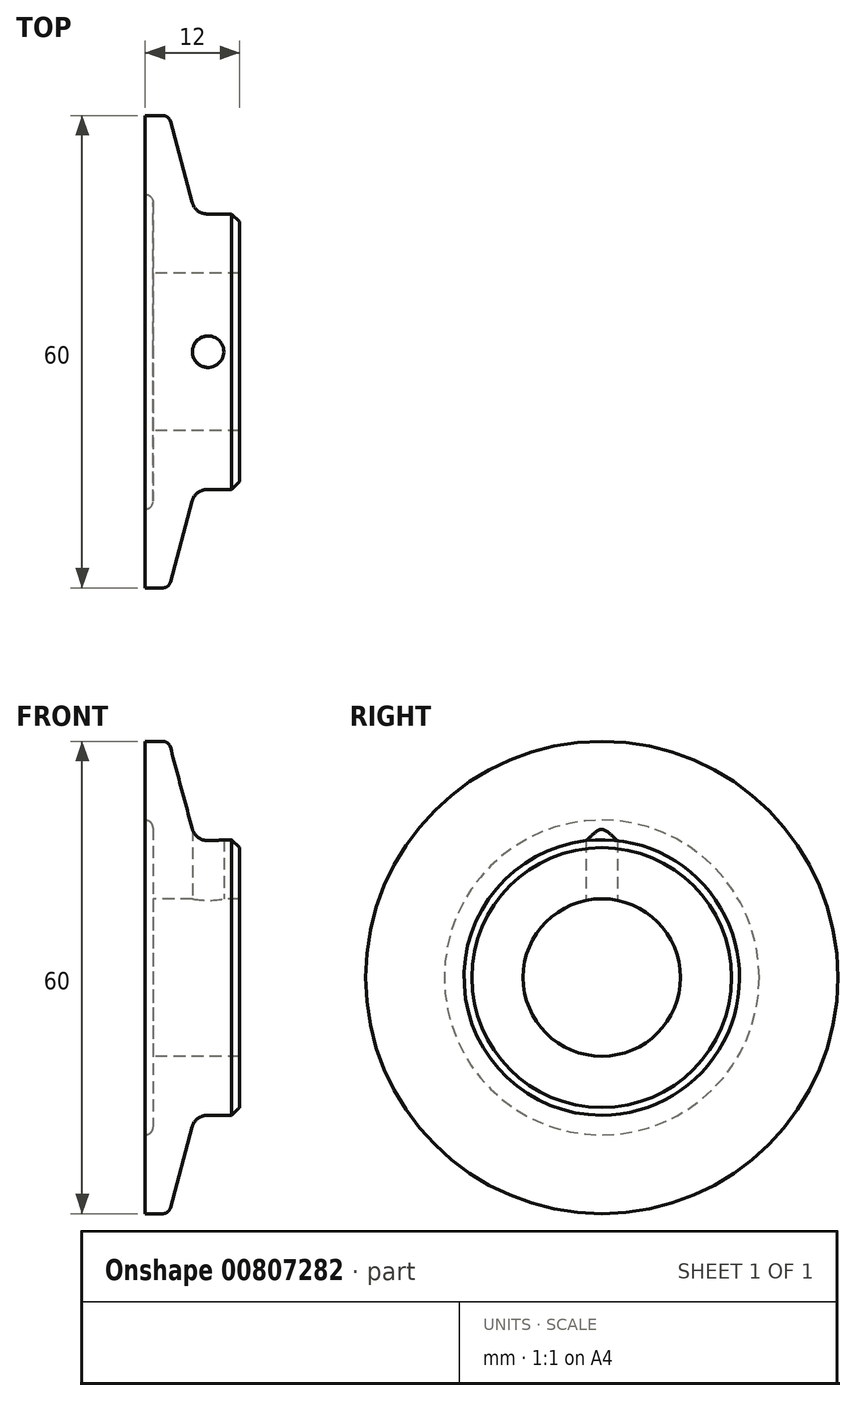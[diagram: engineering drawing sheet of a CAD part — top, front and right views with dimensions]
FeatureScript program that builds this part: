
annotation { "Feature Type Name" : "Feature", "Feature Type Description" : "" }
export const myFeature = defineFeature(function(context is Context, id is Id, definition is map)
    precondition{}
    {
        {
            var Q0;
            Q0=qCreatedBy(makeId("Front.planeOp"),FACE);
            var sketch = newSketch(context, id + "F0", { "sketchPlane" : qUnion([Q0])});
            skLineSegment(sketch, "E0", {"start": v(-9.93, 0) * mm, "end": v(24.3, 0) * mm, "construction": true});
            skLineSegment(sketch, "E1", {"start": v(0, 20) * mm, "end": v(0, 30) * mm});
            skLineSegment(sketch, "E2", {"start": v(0, 30) * mm, "end": v(3, 30) * mm});
            skLineSegment(sketch, "E3", {"start": v(3, 30) * mm, "end": v(6.35, 17.5) * mm});
            skLineSegment(sketch, "E4", {"start": v(6.35, 17.5) * mm, "end": v(12, 17.5) * mm});
            skLineSegment(sketch, "E5", {"start": v(12, 17.5) * mm, "end": v(12, 10) * mm});
            skLineSegment(sketch, "E6", {"start": v(12, 10) * mm, "end": v(1, 10) * mm});
            skLineSegment(sketch, "E7", {"start": v(1, 10) * mm, "end": v(1, 20) * mm});
            skLineSegment(sketch, "E8", {"start": v(1, 20) * mm, "end": v(0, 20) * mm});
            skSolve(sketch);
        }
        {
            var Q0;
            Q0 = qSketchRegion(id + "F0", true);
            var Q1;
            Q1=sQuery(id+"F0.wireOp",EDGE,"E0");
            revolve(context, id + "F1", {"surfaceOperationType" : NewSurfaceOperationType.NEW, "entities" : qUnion([Q0]), "axis" : qUnion([Q1]), "revolveType" : RevolveType.FULL});
        }
        {
            var Q0;
            Q0=makeQuery(id+"F1.opRevolve","SWEPT_EDGE",EDGE,{"disambiguationData":[OSD([sQuery(id+"F0.wireOp",EDGE,"E4"),sQuery(id+"F0.wireOp",EDGE,"E5")])]});
            chamfer(context, id + "F2", {"entities" : qUnion([Q0]), "width" : 1 * mm, "tangentPropagation" : true});
        }
        {
            var Q0;
            Q0=makeQuery(id+"F1.opRevolve","SWEPT_EDGE",EDGE,{"disambiguationData":[OSD([sQuery(id+"F0.wireOp",EDGE,"E2"),sQuery(id+"F0.wireOp",EDGE,"E3")])]});
            var Q1;
            Q1=makeQuery(id+"F1.opRevolve","SWEPT_EDGE",EDGE,{"disambiguationData":[OSD([sQuery(id+"F0.wireOp",EDGE,"E7"),sQuery(id+"F0.wireOp",EDGE,"E8")])]});
            fillet(context, id + "F3", {"entities" : qUnion([Q0, Q1]), "radius" : 1 * mm, "tangentPropagation" : true, "allowEdgeOverflow" : false});
        }
        {
            var Q0;
            Q0=makeQuery(id+"F1.opRevolve","SWEPT_EDGE",EDGE,{"disambiguationData":[OSD([sQuery(id+"F0.wireOp",EDGE,"E3"),sQuery(id+"F0.wireOp",EDGE,"E4")])]});
            fillet(context, id + "F4", {"entities" : qUnion([Q0]), "radius" : 2 * mm, "tangentPropagation" : true, "allowEdgeOverflow" : false});
        }
        {
            var Q0;
            Q0=qCreatedBy(makeId("Top.planeOp"),FACE);
            var sketch = newSketch(context, id + "F5", { "sketchPlane" : qUnion([Q0])});
            skCircle(sketch, "E9", {"center": v(8, 0) * mm, "radius": 2 * mm});
            skSolve(sketch);
        }
        {
            var Q0;
            Q0 = qSketchRegion(id + "F5", true);
            extrude(context, id + "F6", {"entities" : qUnion([Q0]), "operationType" : NewBodyOperationType.REMOVE, "endBound" : BoundingType.THROUGH_ALL, "depth" : 25 * mm, "offsetDistance" : 25 * mm});
        }
    });
